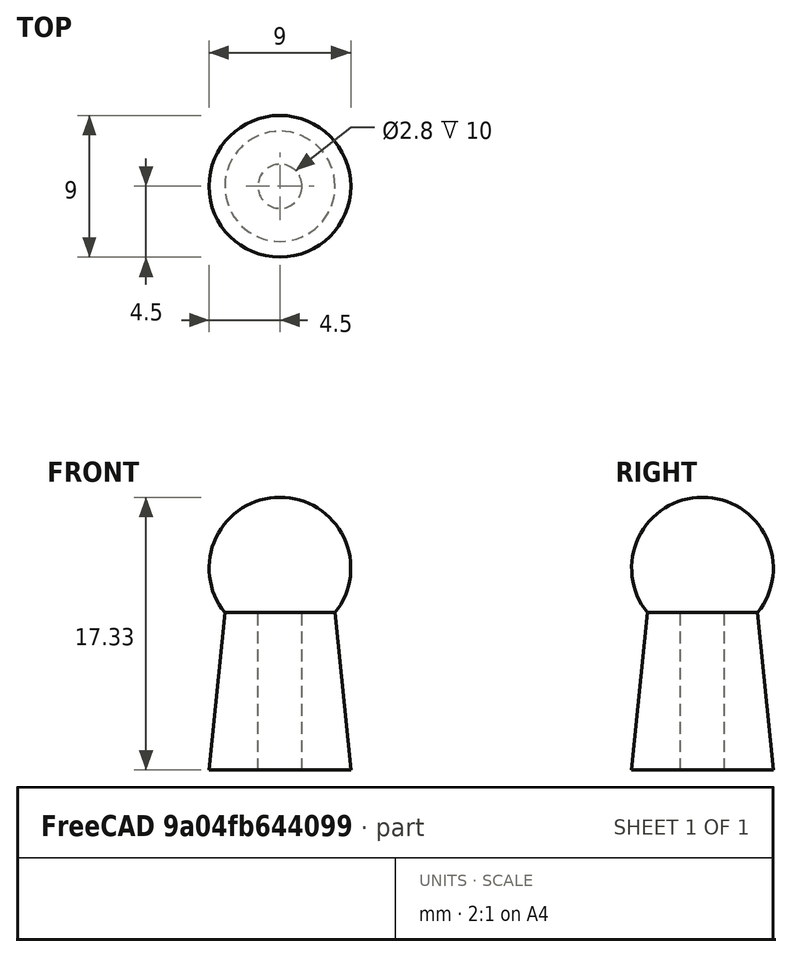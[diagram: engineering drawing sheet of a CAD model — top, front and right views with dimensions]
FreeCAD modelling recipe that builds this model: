
FCSTD DOCUMENT  (FreeCAD 0.14R3702 (Git))
Label: servo-screw-cover
License: CC-BY 3.0
LicenseURL: http://creativecommons.org/licenses/by/3.0/
objects: Sketcher::SketchObject×1, PartDesign::Revolution×1
note: 3 computed .brp shape members not serialized (recipe doc carries the construction recipe); baked Part::Feature solids carry a one-line shape summary decoded from their .brp

FEATURE [Sketcher::SketchObject] Sketch  label="main-body-sketch"
  Placement = pos=(0,0,0) rot=(-1,0,0;4.71239rad)
  sketch-geometry (6):
    g0: LineSegment StartX=1.4 StartY=0 StartZ=0 EndX=4.5 EndY=0 EndZ=0
    g1: LineSegment StartX=4.5 StartY=0 StartZ=0 EndX=3.5 EndY=10 EndZ=0
    g2: LineSegment StartX=1.4 StartY=0 StartZ=0 EndX=1.4 EndY=10 EndZ=0
    g3: LineSegment StartX=1.4 StartY=10 StartZ=0 EndX=0 EndY=10 EndZ=0
    g4: LineSegment StartX=0 StartY=10 StartZ=0 EndX=0 EndY=17.3284 EndZ=0
    g5: ArcOfCircle CenterX=0 CenterY=12.8284 CenterZ=0 NormalX=0 NormalY=0 NormalZ=1 Radius=4.5 StartAngle=5.60351 EndAngle=7.85398
  constraints (19):
    c: Horizontal(g0)
    c: Coincident(g0,g1)
    c: Coincident(g0,g2)
    c: Vertical(g2)
    c: Coincident(g2,g3)
    c: Horizontal(g3)
    c: Coincident(g3,g4)
    c: Vertical(g4)
    c: PointOnObject(g3,g-2)
    c: Coincident(g5,g4)
    c: Coincident(g1,g5)
    c: PointOnObject(g5,g-2)
    c: DistanceX(g-1,g0) = 1.4
    c: PointOnObject(g0,g-1)
    c: DistanceY(g2) = 10
    c: DistanceX(g-1,g0) = 4.5
    c: PointOnObject(g1,g3)
    c: DistanceX(g1,g3) = -3.5
    c: Radius(g5) = 4.5
FEATURE [PartDesign::Revolution] Revolution  label="servo-screw-cover"
  Angle = 360
  Axis = (0,0,1)
  Base = (0,0,0)
  Placement = pos=(0,0,0) rot=(-1,0,0;4.71239rad)
  ReferenceAxis = -> Sketch [V_Axis]
  Reversed = true
  Sketch = -> Sketch
